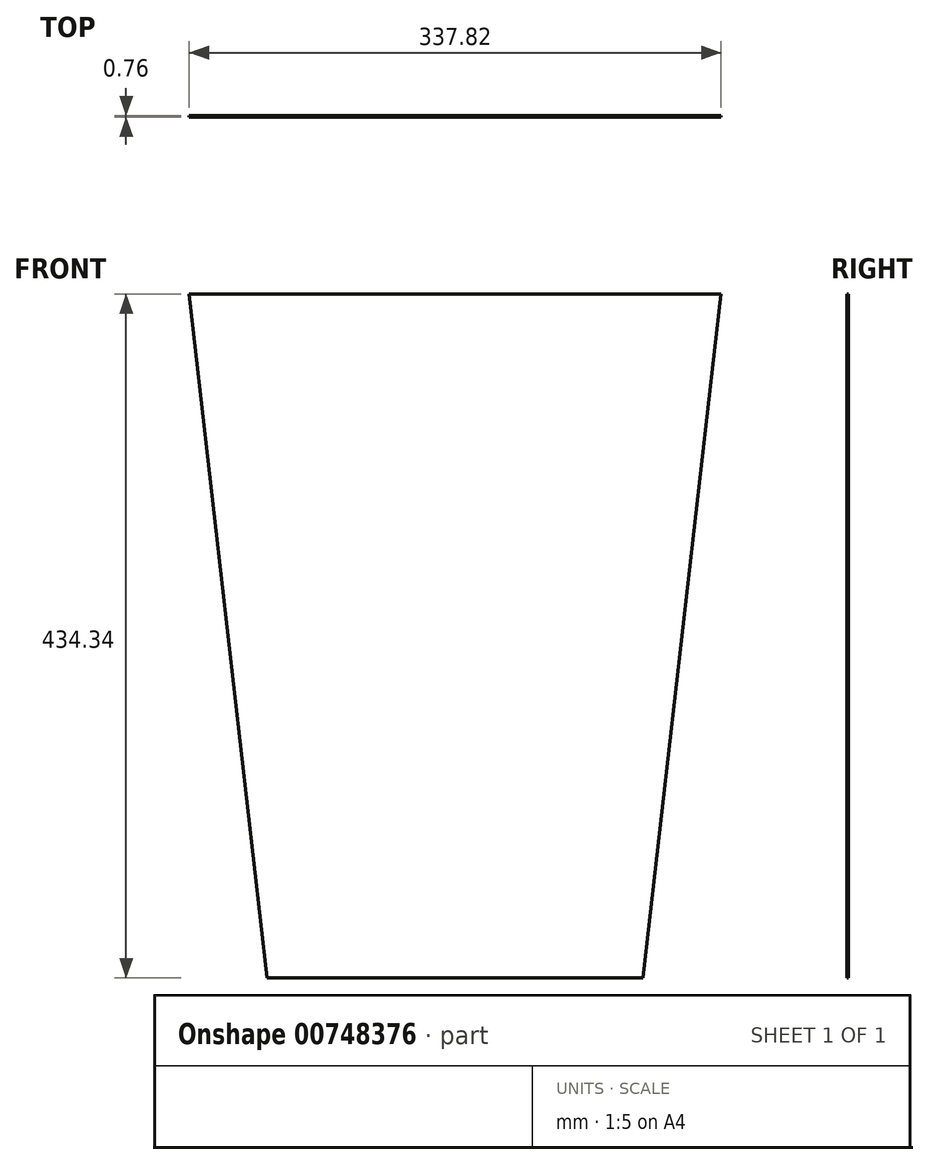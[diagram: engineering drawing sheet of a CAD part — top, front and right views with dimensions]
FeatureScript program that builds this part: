
annotation { "Feature Type Name" : "Feature", "Feature Type Description" : "" }
export const myFeature = defineFeature(function(context is Context, id is Id, definition is map)
    precondition{}
    {
        {
            var Q0;
            Q0=qCreatedBy(makeId("Front.planeOp"),FACE);
            var sketch = newSketch(context, id + "F0", { "sketchPlane" : qUnion([Q0])});
            skLineSegment(sketch, "E0", {"start": v(0, -153.63) * mm, "end": v(-119.38, -153.63) * mm});
            skLineSegment(sketch, "E1", {"start": v(-119.38, -153.63) * mm, "end": v(-168.9, 280.71) * mm});
            skLineSegment(sketch, "E2.MirrorCS", {"start": v(119.38, -153.63) * mm, "end": v(168.9, 280.71) * mm});
            skLineSegment(sketch, "E3.MirrorCS", {"start": v(0, -153.63) * mm, "end": v(119.38, -153.63) * mm});
            skLineSegment(sketch, "E4", {"start": v(-168.91, 280.71) * mm, "end": v(168.91, 280.71) * mm});
            skSolve(sketch);
        }
        {
            var Q0;
            Q0=makeQuery(id+"F0.imprint","IMPRINT",FACE,{"disambiguationData":[TD([[makeQuery(id+"F0.imprint","IMPRINT",EDGE,{"derivedFrom":sQuery(id+"F0.wireOp",EDGE,"E0")}),-1.0]])]});
            extrude(context, id + "F1", {"entities" : qUnion([Q0]), "depth" : 0.76 * mm, "offsetDistance" : 25.4 * mm});
        }
    });
